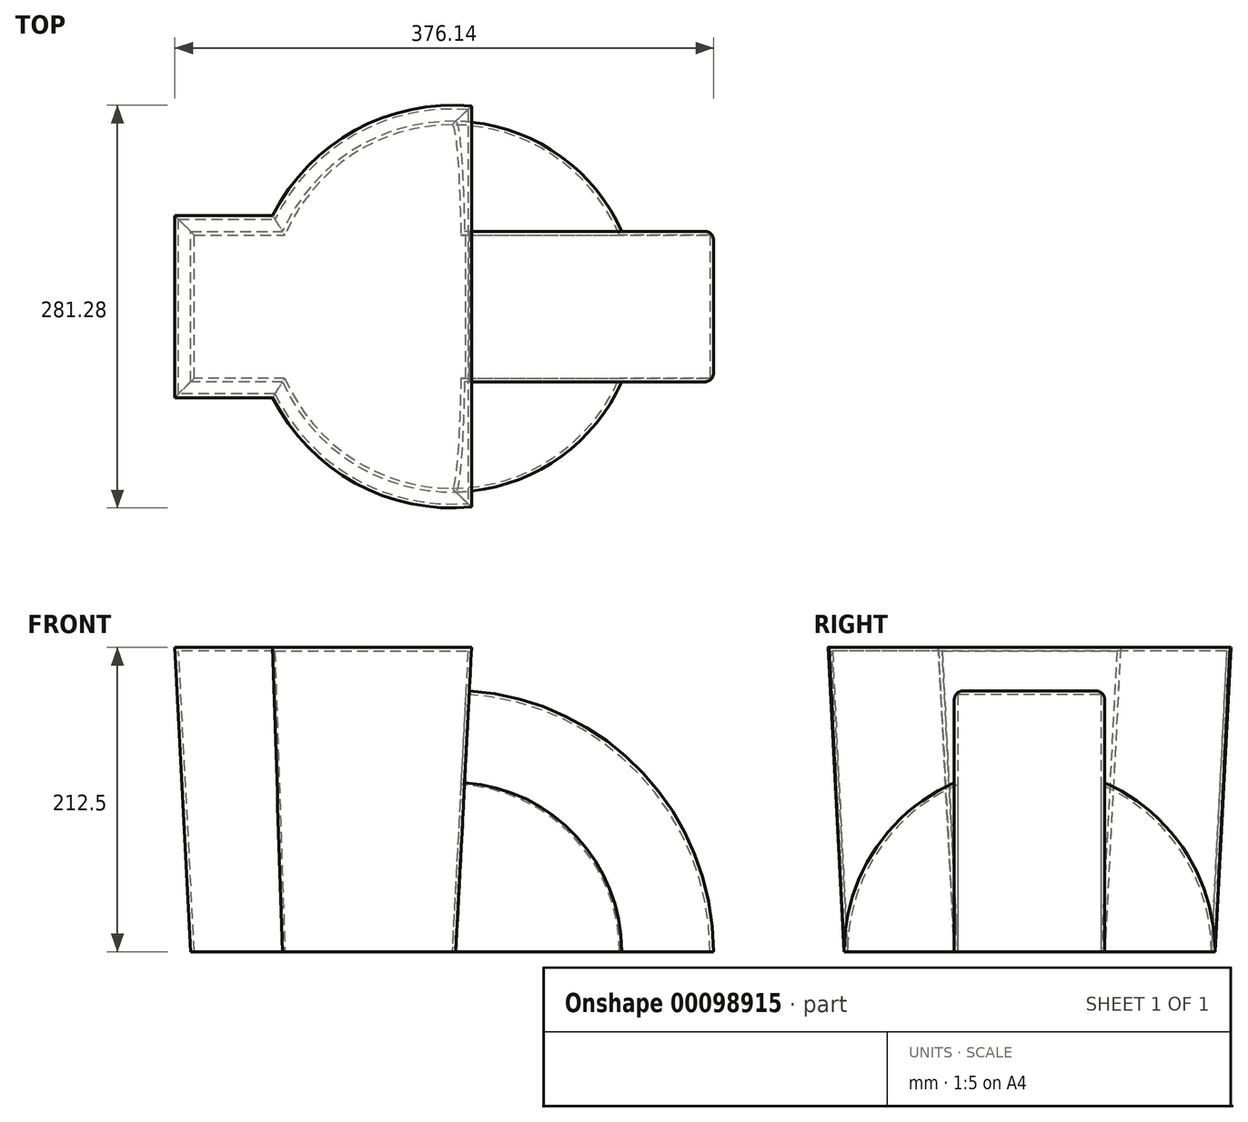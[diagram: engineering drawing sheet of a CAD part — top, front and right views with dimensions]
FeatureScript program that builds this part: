
annotation { "Feature Type Name" : "Feature", "Feature Type Description" : "" }
export const myFeature = defineFeature(function(context is Context, id is Id, definition is map)
    precondition{}
    {
        {
            var Q0;
            Q0=qCreatedBy(makeId("Top.planeOp"),FACE);
            var sketch = newSketch(context, id + "F0", { "sketchPlane" : qUnion([Q0])});
            skCircle(sketch, "E0", {"center": v(0, 0) * mm, "radius": 127 * mm});
            skLineSegment(sketch, "E1.bottom", {"start": v(180, 50) * mm, "end": v(116.74, 50) * mm});
            skLineSegment(sketch, "E1.top", {"start": v(180, -50) * mm, "end": v(116.74, -50) * mm});
            skLineSegment(sketch, "E1.left", {"start": v(180, 50) * mm, "end": v(180, -50) * mm});
            skLineSegment(sketch, "E1.right", {"start": v(-180, 50) * mm, "end": v(-180, -50) * mm});
            skLineSegment(sketch, "E2.trimOffspring", {"start": v(-116.74, 50) * mm, "end": v(-180, 50) * mm});
            skLineSegment(sketch, "E3.trimOffspring", {"start": v(-116.74, -50) * mm, "end": v(-180, -50) * mm});
            skLineSegment(sketch, "E4", {"start": v(0, 127) * mm, "end": v(0, -127) * mm});
            skSolve(sketch);
        }
        {
            var Q0;
            Q0=makeQuery(id+"F0.imprint","IMPRINT",FACE,{"disambiguationData":[TD([[makeQuery(id+"F0.imprint","IMPRINT",EDGE,{"derivedFrom":sQuery(id+"F0.wireOp",EDGE,"E1.right")}),1.0]])]});
            var Q1;
            {var subQ2=sQuery(id+"F0.wireOp",EDGE,"E4");Q1=makeQuery(id+"F0.imprint","IMPRINT",FACE,{"disambiguationData":[TD([[makeQuery(id+"F0.imprint","IMPRINT",EDGE,{"derivedFrom":subQ2}),-1.0]])]});}
            extrude(context, id + "F1", {"entities" : qUnion([Q0, Q1]), "depth" : 210 * mm, "hasDraft" : true, "draftAngle" : 3 * degree});
        }
        {
            var Q0;
            {var subQ2=sQuery(id+"F0.wireOp",EDGE,"E4");Q0=makeQuery(id+"F0.imprint","IMPRINT",FACE,{"disambiguationData":[TD([[makeQuery(id+"F0.imprint","IMPRINT",EDGE,{"derivedFrom":subQ2}),1.0]])]});}
            var Q1;
            {var subQ0=sQuery(id+"F0.wireOp",EDGE,"E1.bottom");Q1=makeQuery(id+"F0.imprint","IMPRINT",FACE,{"disambiguationData":[TD([[makeQuery(id+"F0.imprint","IMPRINT",EDGE,{"derivedFrom":subQ0}),1.0]])]});}
            var Q2;
            Q2=sQuery(id+"F0.wireOp",EDGE,"E4");
            revolve(context, id + "F2", {"operationType" : NewBodyOperationType.ADD, "entities" : qUnion([Q0, Q1]), "axis" : qUnion([Q2]), "revolveType" : RevolveType.ONE_DIRECTION, "angle" : 90 * degree});
        }
        {
            var Q0;
            {var subQ0=sQuery(id+"F0.wireOp",EDGE,"E4");var subQ1=sQuery(id+"F0.wireOp",EDGE,"E0");Q0=makeQuery(id+"F2.boolean.opBoolean","MERGE",FACE,{"derivedFrom":[makeQuery(id+"F1.opExtrude","CAP_FACE",FACE,{"disambiguationData":[OSD([subQ1,sQuery(id+"F0.wireOp",EDGE,"E1.right"),sQuery(id+"F0.wireOp",EDGE,"E2.trimOffspring"),sQuery(id+"F0.wireOp",EDGE,"E3.trimOffspring"),subQ0])],"isStart":true}),makeQuery(id+"F2.opRevolve","CAP_FACE",FACE,{"disambiguationData":[OSD([subQ1,sQuery(id+"F0.wireOp",EDGE,"E1.bottom"),sQuery(id+"F0.wireOp",EDGE,"E1.top"),sQuery(id+"F0.wireOp",EDGE,"E1.left"),subQ0])],"isStart":true})]});}
            shell(context, id + "F3", {"entities" : qUnion([Q0]), "thickness" : 2.5 * mm, "oppositeDirection" : true});
        }
        {
            var Q0;
            Q0=makeQuery(id+"F2.opRevolve","SWEPT_EDGE",EDGE,{"disambiguationData":[OSD([sQuery(id+"F0.wireOp",EDGE,"E1.top"),sQuery(id+"F0.wireOp",EDGE,"E1.left")])]});
            var Q1;
            Q1=makeQuery(id+"F2.opRevolve","SWEPT_EDGE",EDGE,{"disambiguationData":[OSD([sQuery(id+"F0.wireOp",EDGE,"E1.bottom"),sQuery(id+"F0.wireOp",EDGE,"E1.left")])]});
            fillet(context, id + "F4", {"entities" : qUnion([Q0, Q1]), "radius" : 6 * mm, "tangentPropagation" : true, "allowEdgeOverflow" : false});
        }
    });
